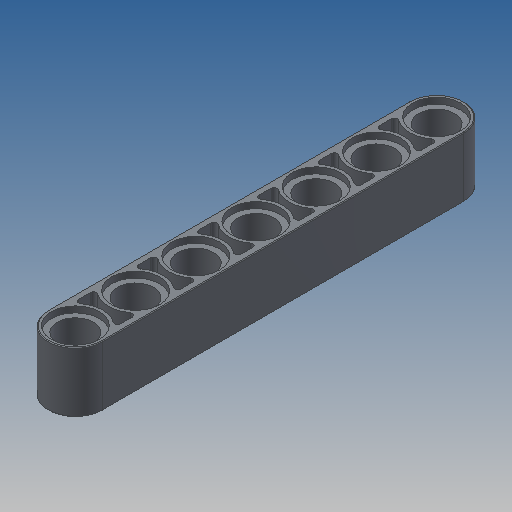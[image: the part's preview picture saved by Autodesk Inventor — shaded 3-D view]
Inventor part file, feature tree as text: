
AUTODESK INVENTOR PART (.ipt)
format: ipt  version: 2022.2 (Build 262287000, 287)  size: 357,376 bytes
history: native  units: mm
features: extrude x3, sketch x2, mirror x1, fillet x1
ambient origin geometry x8: Origin, YZ Plane, XZ Plane, XY Plane, X Axis, Y Axis, Z Axis, Center Point
bodies: Solid1 (feature_tree)
feature tree (7):
  extrude  "Extrusion1"  Depth=7.2mm
  sketch  "Sketch6"  dims[d41=0.8mm d42=0.0mm d43=3.1mm d44=0.0mm d48=48.0mm d49=6.4mm d50=4.8mm d51=8.0mm d52=0.8mm d53=60.0mm d55=8.0mm d56=10.0mm d58=10.0mm d60=0.4mm d61=0.1mm]
  extrude  "Extrusion7"  Depth=3.1mm TaperAngle=0.0deg
  extrude  "Extrusion8"  Depth=0.1mm
  mirror  "Mirror1"
  fillet  "Fillet2"  Radius=6.4mm
  sketch  "Sketch1"  dims[d14=8.0mm d15=0.0mm d32=7.2mm]
